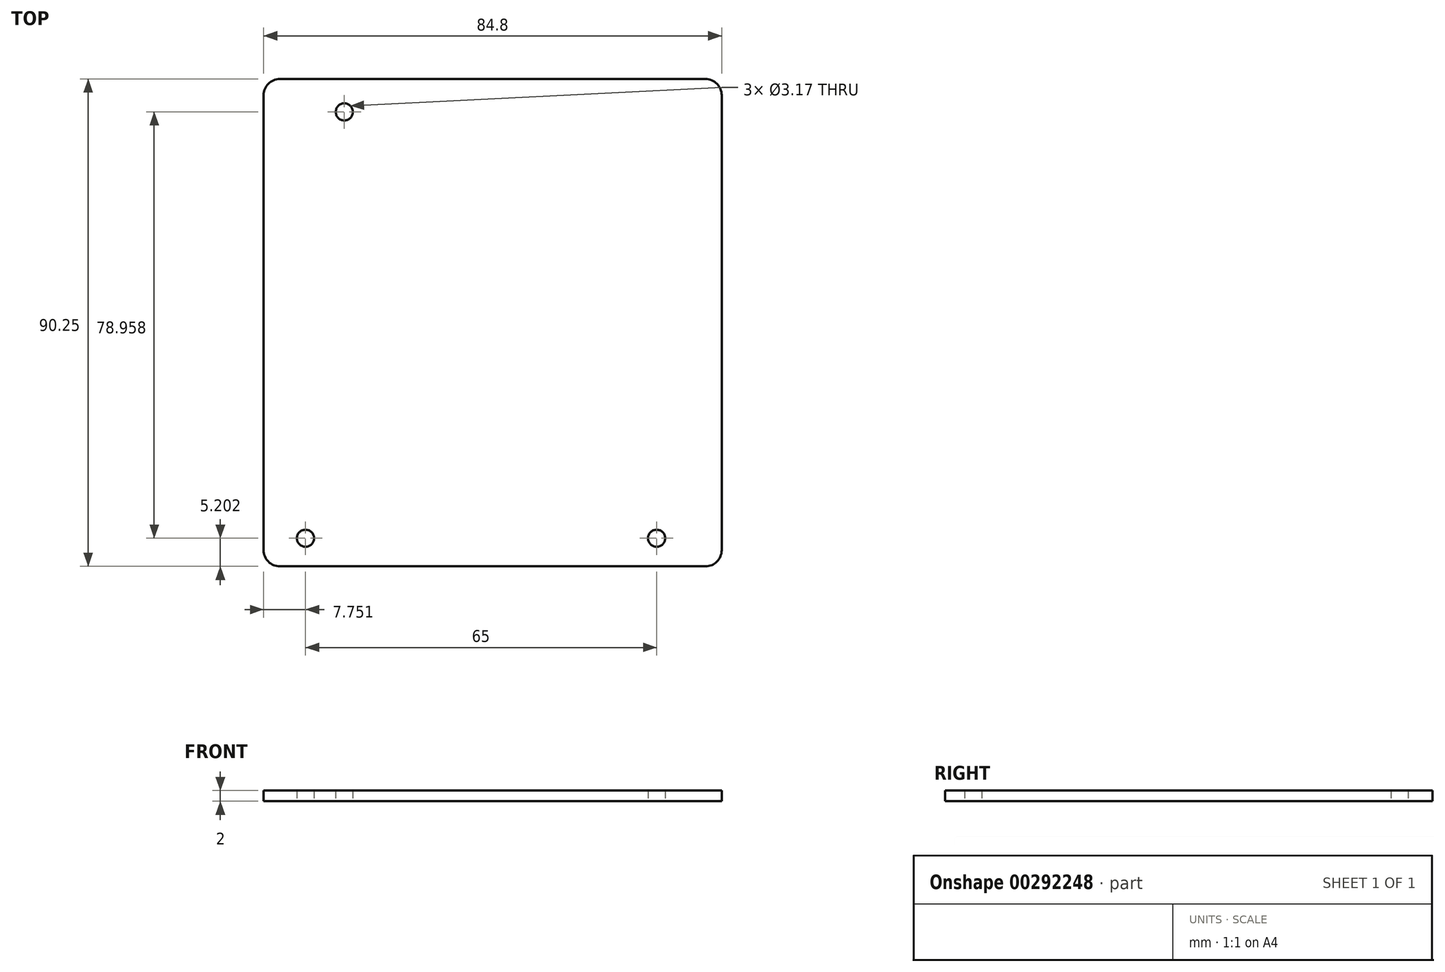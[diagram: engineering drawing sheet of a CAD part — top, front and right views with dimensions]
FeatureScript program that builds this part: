
annotation { "Feature Type Name" : "Feature", "Feature Type Description" : "" }
export const myFeature = defineFeature(function(context is Context, id is Id, definition is map)
    precondition{}
    {
        {
            var Q0;
            Q0=qCreatedBy(makeId("Top.planeOp"),FACE);
            var sketch = newSketch(context, id + "F0", { "sketchPlane" : qUnion([Q0])});
            skLineSegment(sketch, "E0.bottom", {"start": v(-55.4, 50.07) * mm, "end": v(23.4, 50.07) * mm});
            skLineSegment(sketch, "E0.top", {"start": v(-55.4, -40.18) * mm, "end": v(23.4, -40.18) * mm});
            skLineSegment(sketch, "E0.left", {"start": v(-58.4, 47.07) * mm, "end": v(-58.4, -37.18) * mm});
            skLineSegment(sketch, "E0.right", {"start": v(26.4, 47.07) * mm, "end": v(26.4, -40.18) * mm});
            skPoint(sketch, "E0.middle", {"position": v(-16, 4.94) * mm});
            skLineSegment(sketch, "E1", {"start": v(26.4, -37.18) * mm, "end": v(26.4, -34.98) * mm});
            skLineSegment(sketch, "E2", {"start": v(26.4, -34.98) * mm, "end": v(14.36, -34.98) * mm});
            skCircle(sketch, "E3", {"center": v(14.36, -34.98) * mm, "radius": 1.59 * mm});
            skLineSegment(sketch, "E4", {"start": v(14.36, -34.98) * mm, "end": v(-50.64, -34.98) * mm});
            skCircle(sketch, "E5", {"center": v(-50.64, -34.98) * mm, "radius": 1.59 * mm});
            skLineSegment(sketch, "E6", {"start": v(-50.64, -34.98) * mm, "end": v(-50.64, 43.98) * mm});
            skLineSegment(sketch, "E7", {"start": v(-50.64, 43.98) * mm, "end": v(-43.46, 43.98) * mm});
            skCircle(sketch, "E8", {"center": v(-43.46, 43.98) * mm, "radius": 1.59 * mm});
            skPoint(sketch, "E9.visualSharp", {"position": v(-58.4, 50.07) * mm});
            skArc(sketch, "E9.filletArc", {"start": v(-55.4, 50.07) * mm, "mid": v(-57.52, 49.19) * mm, "end": v(-58.4, 47.07) * mm});
            skPoint(sketch, "E10.visualSharp", {"position": v(26.4, 50.07) * mm});
            skArc(sketch, "E10.filletArc", {"start": v(26.4, 47.07) * mm, "mid": v(25.53, 49.19) * mm, "end": v(23.4, 50.07) * mm});
            skPoint(sketch, "E11.visualSharp", {"position": v(26.4, -40.18) * mm});
            skArc(sketch, "E11.filletArc", {"start": v(23.4, -40.18) * mm, "mid": v(25.53, -39.3) * mm, "end": v(26.4, -37.18) * mm});
            skPoint(sketch, "E12.visualSharp", {"position": v(-58.4, -40.18) * mm});
            skArc(sketch, "E12.filletArc", {"start": v(-58.4, -37.18) * mm, "mid": v(-57.52, -39.3) * mm, "end": v(-55.4, -40.18) * mm});
            skSolve(sketch);
        }
        {
            var Q0;
            Q0 = qSketchRegion(id + "F0", true);
            extrude(context, id + "F1", {"entities" : qUnion([Q0]), "depth" : 2 * mm});
        }
    });
